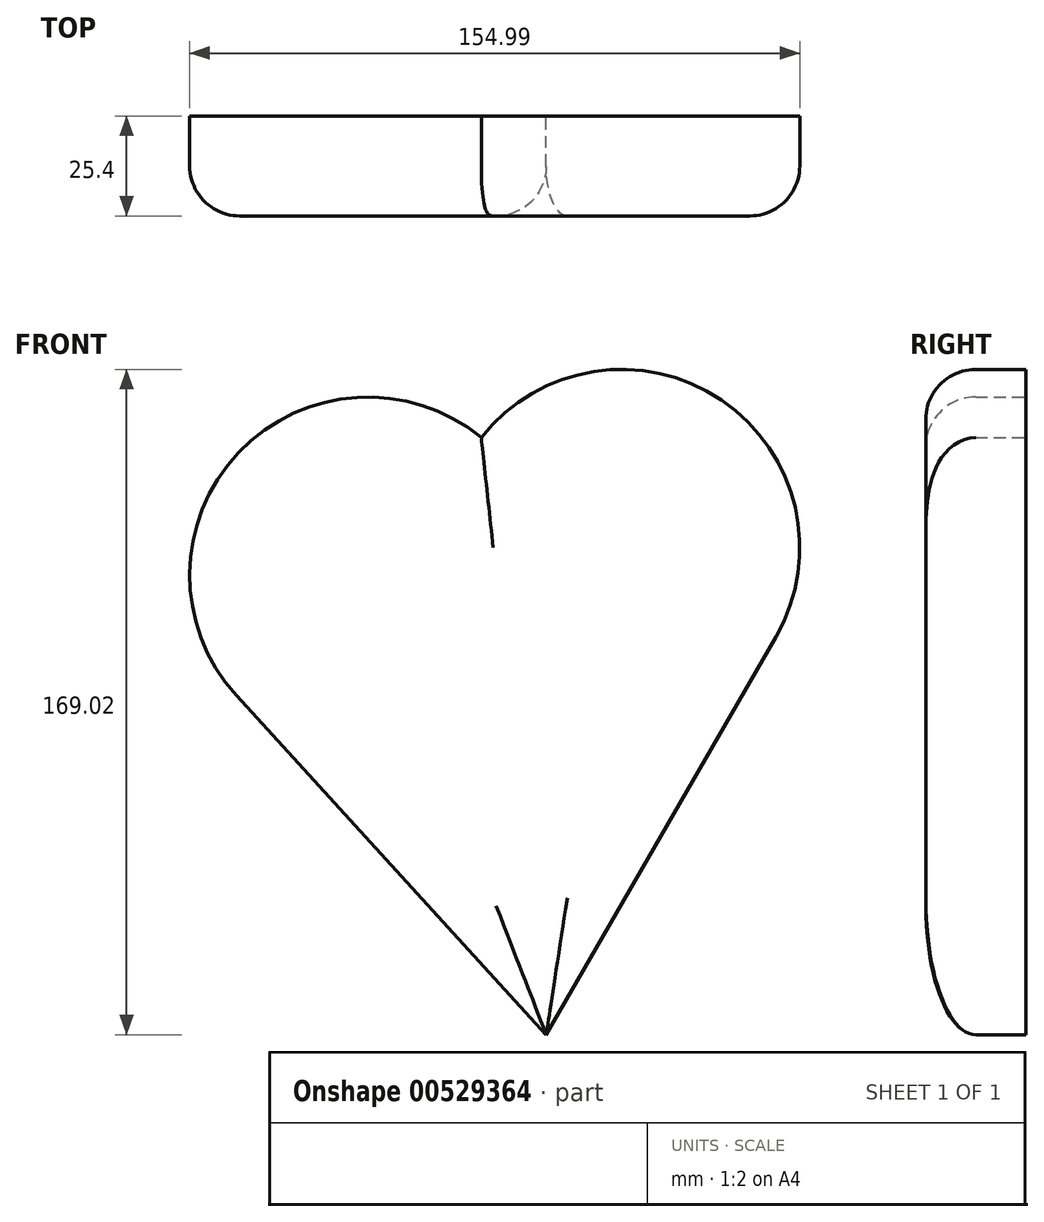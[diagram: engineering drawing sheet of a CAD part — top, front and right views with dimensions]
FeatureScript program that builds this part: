
annotation { "Feature Type Name" : "Feature", "Feature Type Description" : "" }
export const myFeature = defineFeature(function(context is Context, id is Id, definition is map)
    precondition{}
    {
        {
            var Q0;
            Q0=qCreatedBy(makeId("Front.planeOp"),FACE);
            var sketch = newSketch(context, id + "F0", { "sketchPlane" : qUnion([Q0])});
            skCircle(sketch, "E0", {"center": v(-30.18, 39.27) * mm, "radius": 45.3 * mm});
            skLineSegment(sketch, "E1", {"start": v(15.1, -77.45) * mm, "end": v(-63.62, 8.72) * mm});
            skLineSegment(sketch, "E2", {"start": v(15.1, 39.27) * mm, "end": v(15.1, -77.45) * mm});
            skPoint(sketch, "E3.MirrorCS.end.orphan", {"position": v(93.83, 8.72) * mm});
            skPoint(sketch, "E3.MirrorCS.start.orphan", {"position": v(15.1, -77.45) * mm});
            skSolve(sketch);
        }
        {
            var Q0;
            {var subQ0=sQuery(id+"F0.wireOp",EDGE,"E0");var subQ1=makeQuery(id+"F0.imprint","INTERSECT",VERTEX,{"derivedFrom":[subQ0,sQuery(id+"F0.wireOp",EDGE,"E1")]});Q0=makeQuery(id+"F0.imprint","IMPRINT",FACE,{"disambiguationData":[TD([[makeQuery(id+"F0.imprint","IMPRINT",EDGE,{"disambiguationData":[TD([[subQ1,1.0]])],"derivedFrom":subQ0}),1.0]])]});}
            var Q1;
            {var subQ0=sQuery(id+"F0.wireOp",EDGE,"bbabedca-f16b-4829-a472-ff1ed118b1d90.MirrorC");var subQ1=makeQuery(id+"F0.imprint","INTERSECT",VERTEX,{"derivedFrom":[subQ0,sQuery(id+"F0.wireOp",EDGE,"E3.MirrorCS")]});Q1=makeQuery(id+"F0.imprint","IMPRINT",FACE,{"disambiguationData":[TD([[makeQuery(id+"F0.imprint","IMPRINT",EDGE,{"disambiguationData":[TD([[subQ1,1.0]])],"derivedFrom":subQ0}),-1.0]])]});}
            var Q2;
            {var subQ0=sQuery(id+"F0.wireOp",EDGE,"E1");Q2=makeQuery(id+"F0.imprint","IMPRINT",FACE,{"disambiguationData":[TD([[makeQuery(id+"F0.imprint","IMPRINT",EDGE,{"derivedFrom":subQ0}),-1.0]])]});}
            extrude(context, id + "F1", {"entities" : qUnion([Q0, Q1, Q2]), "depth" : 25.4 * mm, "offsetDistance" : 25.4 * mm});
        }
        {
            var Q0;
            Q0=makeQuery(id+"F1.opExtrude","CAP_FACE",FACE,{"disambiguationData":[OSD([sQuery(id+"F0.wireOp",EDGE,"E0"),sQuery(id+"F0.wireOp",EDGE,"E1"),sQuery(id+"F0.wireOp",EDGE,"E2")])],"isStart":false});
            fillet(context, id + "F2", {"entities" : qUnion([Q0]), "radius" : 12.7 * mm, "tangentPropagation" : true, "allowEdgeOverflow" : false});
        }
        {
            var Q0;
            {var subQ0=sQuery(id+"F0.wireOp",EDGE,"E2");var subQ1=sQuery(id+"F0.wireOp",EDGE,"E1");Q0=makeQuery(id+"F2.opFillet","BLEND_VERTEX",VERTEX,{"blendedFrom":[makeQuery(id+"F1.opExtrude","CAP_EDGE",EDGE,{"disambiguationData":[OSD([subQ1])],"isStart":false}),makeQuery(id+"F1.opExtrude","CAP_EDGE",EDGE,{"disambiguationData":[OSD([subQ0])],"isStart":false}),makeQuery(id+"F1.opExtrude","SWEPT_FACE",FACE,{"disambiguationData":[OSD([subQ1])]}),makeQuery(id+"F1.opExtrude","SWEPT_FACE",FACE,{"disambiguationData":[OSD([subQ0])]})],"blendedInto":[makeQuery(id+"F1.opExtrude","SWEPT_FACE",FACE,{"disambiguationData":[OSD([subQ1])]}),makeQuery(id+"F1.opExtrude","SWEPT_FACE",FACE,{"disambiguationData":[OSD([subQ0])]})]});}
            var Q1;
            Q1=makeQuery(id+"F1.opExtrude","CAP_VERTEX",VERTEX,{"disambiguationData":[OSD([sQuery(id+"F0.wireOp",EDGE,"E1"),sQuery(id+"F0.wireOp",EDGE,"E2")])],"isStart":true});
            var Q2;
            {var subQ0=sQuery(id+"F0.wireOp",EDGE,"E2");var subQ1=sQuery(id+"F0.wireOp",EDGE,"E0");Q2=makeQuery(id+"F2.opFillet","BLEND_VERTEX",VERTEX,{"blendedFrom":[makeQuery(id+"F1.opExtrude","CAP_EDGE",EDGE,{"disambiguationData":[OSD([subQ1])],"isStart":false}),makeQuery(id+"F1.opExtrude","CAP_EDGE",EDGE,{"disambiguationData":[OSD([subQ0])],"isStart":false}),makeQuery(id+"F1.opExtrude","CAP_FACE",FACE,{"disambiguationData":[OSD([subQ1,sQuery(id+"F0.wireOp",EDGE,"E1"),subQ0])],"isStart":false})],"blendedInto":[makeQuery(id+"F1.opExtrude","CAP_FACE",FACE,{"disambiguationData":[OSD([subQ1,sQuery(id+"F0.wireOp",EDGE,"E1"),subQ0])],"isStart":false})]});}
            cPlane(context, id + "F3", {"entities" : qUnion([Q0, Q1, Q2]), "cplaneType" : CPlaneType.THREE_POINT, "offset" : 25.4 * mm, "width" : 152.4 * mm, "height" : 152.4 * mm});
        }
        {
            var Q0;
            Q0=makeQuery(id+"F1.opExtrude","SWEPT_BODY",BODY,{"disambiguationData":[OSD([sQuery(id+"F0.wireOp",EDGE,"E0"),sQuery(id+"F0.wireOp",EDGE,"E1"),sQuery(id+"F0.wireOp",EDGE,"E2")])]});
            var Q1;
            Q1=qCreatedBy(id+"F3.planeOp",FACE);
            mirror(context, id + "F4", {"operationType" : NewBodyOperationType.ADD, "entities" : qUnion([Q0]), "mirrorPlane" : qUnion([Q1])});
        }
        {
            var Q1;
            Q1=makeQuery(id+"F2.opFillet","BLEND_FACE",FACE,{"disambiguationData":[OSD([sQuery(id+"F0.wireOp",EDGE,"E2")])]});
            var Q2;
            Q2=makeQuery(id+"F4.opPattern","COPY",FACE,{"derivedFrom":makeQuery(id+"F2.opFillet","BLEND_FACE",FACE,{"disambiguationData":[OSD([sQuery(id+"F0.wireOp",EDGE,"E2")])]}),"instanceName":"1"});
            loft(context, id + "F5", {"operationType" : NewBodyOperationType.ADD, "sheetProfilesArray" : [{ "sheetProfileEntities" : qUnion([Q1]) }, { "sheetProfileEntities" : qUnion([Q2]) }]});
        }
    });
